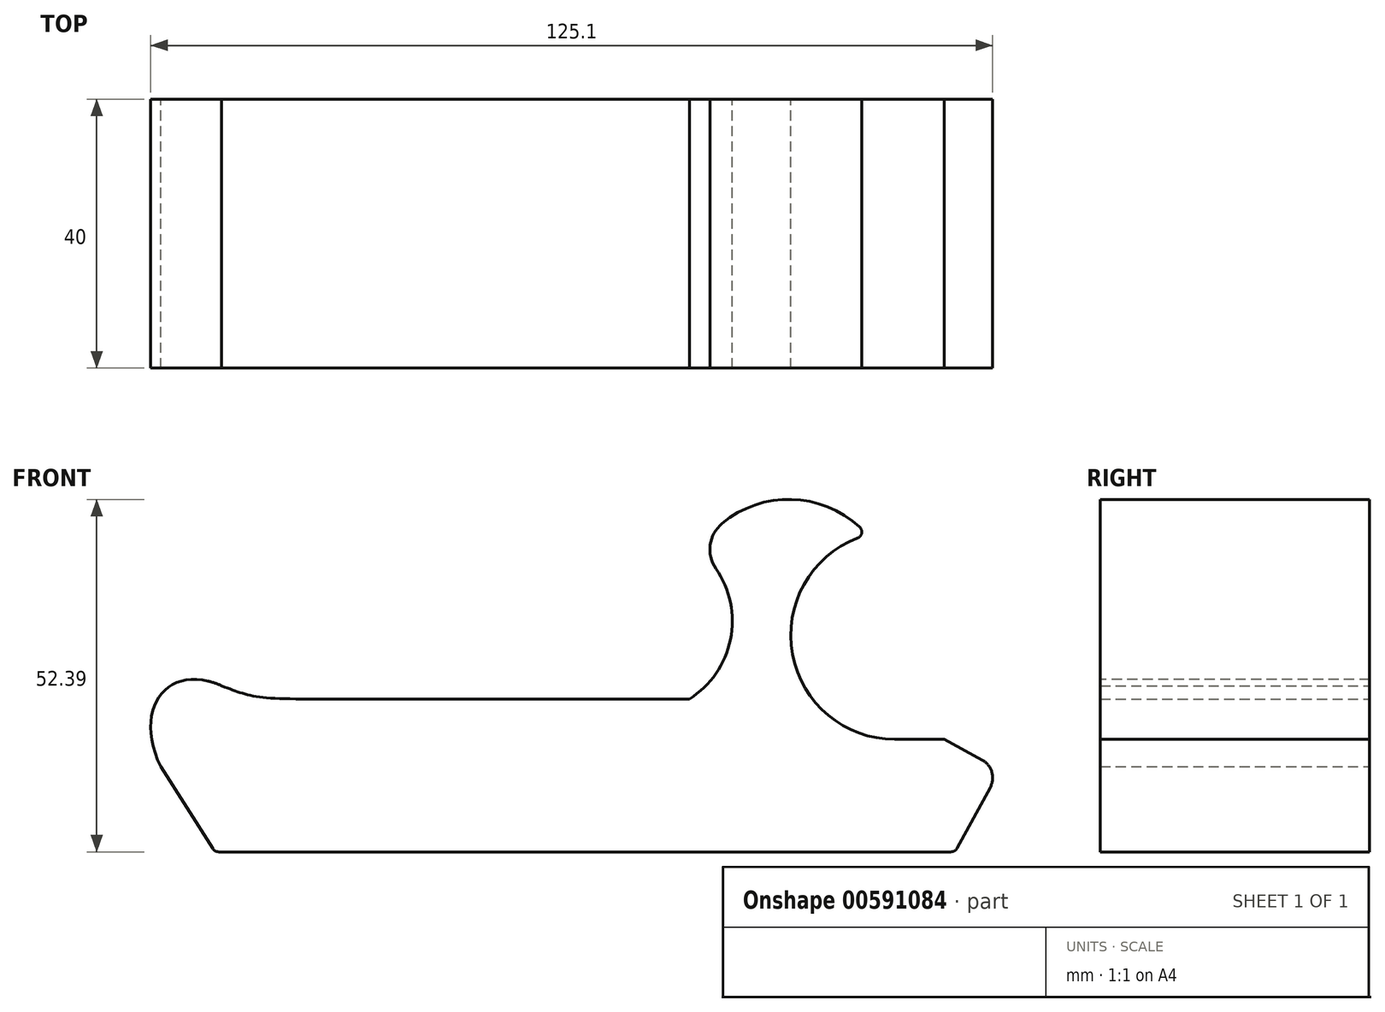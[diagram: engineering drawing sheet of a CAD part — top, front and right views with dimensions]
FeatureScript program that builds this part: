
annotation { "Feature Type Name" : "Feature", "Feature Type Description" : "" }
export const myFeature = defineFeature(function(context is Context, id is Id, definition is map)
    precondition{}
    {
        {
            var Q0;
            Q0=qCreatedBy(makeId("Front.planeOp"),FACE);
            var sketch = newSketch(context, id + "F0", { "sketchPlane" : qUnion([Q0])});
            skLineSegment(sketch, "E0", {"start": v(49.84, -22.73) * mm, "end": v(-59.02, -22.73) * mm});
            skLineSegment(sketch, "E1", {"start": v(-59.86, -22.26) * mm, "end": v(-67.61, -10.07) * mm});
            skFitSpline(sketch, "E2", {"points": [v(-67.61, -10.07) * mm, v(-55.36, 0) * mm], "startDerivative": vector(-14.43, 30.2) * mm, "endDerivative": vector(28.3, -21.67) * mm});
            skLineSegment(sketch, "E3", {"start": v(0, 0) * mm, "end": v(-55.36, 0) * mm});
            skFitSpline(sketch, "E4", {"points": [v(-60.6, 2.66) * mm, v(-46.62, 0) * mm], "startDerivative": vector(15.87, -5.21) * mm, "endDerivative": vector(26.25, 0) * mm});
            skArc(sketch, "E5", {"start": v(10.92, 0) * mm, "mid": v(17.05, 8.84) * mm, "end": v(14.88, 19.38) * mm});
            skLineSegment(sketch, "E6", {"start": v(10.92, 0) * mm, "end": v(0, 0) * mm});
            skArc(sketch, "E7", {"start": v(36.23, 25.56) * mm, "mid": v(26.1, 29.66) * mm, "end": v(15.8, 26.08) * mm});
            skLineSegment(sketch, "E8", {"start": v(50.72, -22.2) * mm, "end": v(55.64, -13.15) * mm});
            skLineSegment(sketch, "E9", {"start": v(54.43, -9.08) * mm, "end": v(48.77, -6) * mm});
            skLineSegment(sketch, "E10", {"start": v(48.77, -6) * mm, "end": v(41.46, -6) * mm});
            skArc(sketch, "E11", {"start": v(35.91, 23.89) * mm, "mid": v(26.26, 6.64) * mm, "end": v(41.46, -6) * mm});
            skPoint(sketch, "E12.visualSharp", {"position": v(12.39, 22.1) * mm});
            skArc(sketch, "E12.filletArc", {"start": v(15.8, 26.08) * mm, "mid": v(14.03, 22.9) * mm, "end": v(14.88, 19.38) * mm});
            skPoint(sketch, "E13.visualSharp", {"position": v(37.39, 24.37) * mm});
            skArc(sketch, "E13.filletArc", {"start": v(35.91, 23.89) * mm, "mid": v(36.53, 24.64) * mm, "end": v(36.23, 25.56) * mm});
            skPoint(sketch, "E14.visualSharp", {"position": v(57.07, -10.5) * mm});
            skArc(sketch, "E14.filletArc", {"start": v(55.64, -13.15) * mm, "mid": v(55.88, -10.86) * mm, "end": v(54.43, -9.08) * mm});
            skPoint(sketch, "E15.visualSharp", {"position": v(-59.57, -22.73) * mm});
            skArc(sketch, "E15.filletArc", {"start": v(-59.86, -22.26) * mm, "mid": v(-59.5, -22.6) * mm, "end": v(-59.02, -22.73) * mm});
            skPoint(sketch, "E16.visualSharp", {"position": v(50.43, -22.73) * mm});
            skArc(sketch, "E16.filletArc", {"start": v(49.84, -22.73) * mm, "mid": v(50.35, -22.58) * mm, "end": v(50.72, -22.2) * mm});
            skSolve(sketch);
        }
        {
            var Q0;
            Q0 = qSketchRegion(id + "F0", true);
            extrude(context, id + "F1", {"entities" : qUnion([Q0]), "depth" : 40 * mm, "offsetDistance" : 25 * mm});
        }
    });
